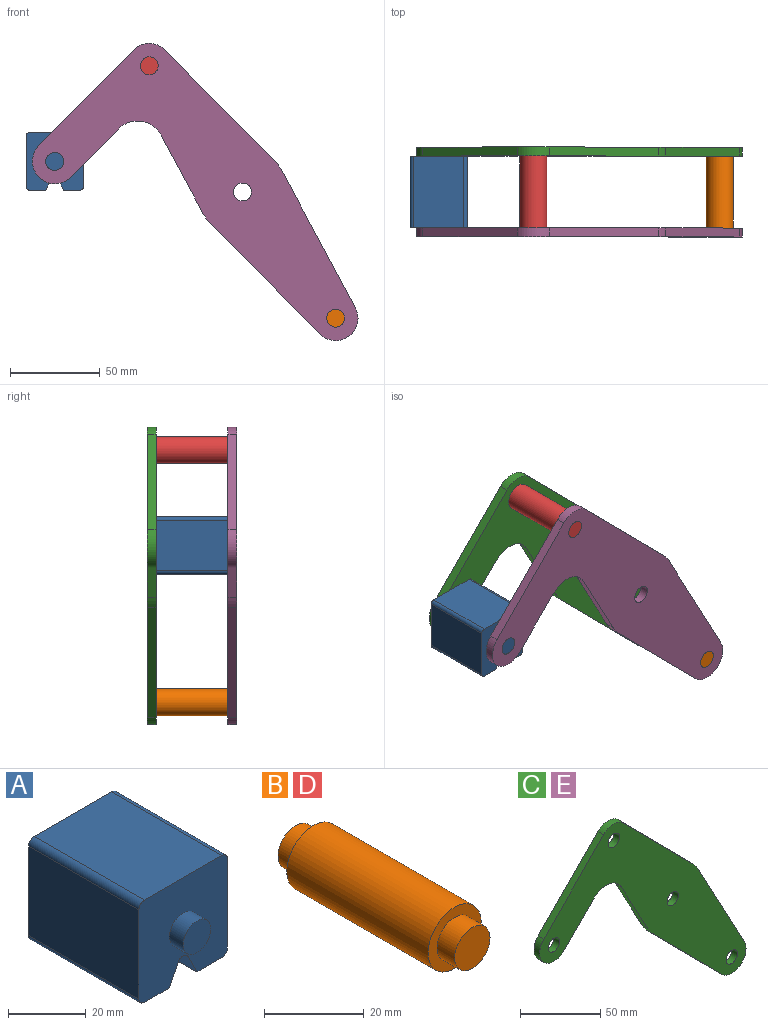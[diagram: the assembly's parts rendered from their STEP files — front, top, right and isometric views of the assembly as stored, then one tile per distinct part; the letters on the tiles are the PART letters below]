
ASSEMBLY  parts=5 mates=3
PART A: 18 faces, bbox 32.1x50x32.1 mm
  f0: plane 40x28.08mm, normal (1,0,0), area 1123.1mm2, adj f4,f10,f13,f14
  f1: plane 40x9.04mm, normal (0,0,-1), area 361.6mm2, adj f2,f4,f10,f14
  f2: plane 40x6.42mm, normal (-0.89,0,-0.45), area 287.2mm2, adj f1,f4,f10,f15
  f3: plane 40x6.42mm, normal (0.89,0,-0.45), area 287.2mm2, adj f4,f5,f10,f15
  f4: plane 32.08x32.08mm, normal (0,-1,0), area 900.6mm2, adj f0,f1,f2,f3,f5,f6,f7,f9
  f5: plane 40x9.04mm, normal (0,0,-1), area 361.6mm2, adj f3,f4,f10,f16
  f6: plane 40x28.08mm, normal (0,0,1), area 1123.1mm2, adj f4,f10,f13,f17
  f7: plane 40x28.08mm, normal (-1,0,0), area 1123.1mm2, adj f4,f10,f16,f17
  f8: plane 10x10mm, normal (0,-1,0), area 78.5mm2, adj f9
  f9: cylinder r=5mm len=10mm, axis (0,1,0), area 157.1mm2, adj f4,f8
  f10: plane 32.08x32.08mm, normal (0,1,0), area 900.6mm2, adj f0,f1,f2,f3,f5,f6,f7,f12
  f11: plane 10x10mm, normal (0,1,0), area 78.5mm2, adj f12
  f12: cylinder r=5mm len=10mm, axis (0,-1,0), area 157.1mm2, adj f10,f11
  f13: cylinder r=2mm len=40mm, axis (0,1,0), area 125.7mm2, adj f0,f4,f6,f10
  f14: cylinder r=2mm len=40mm, axis (0,-1,0), area 125.7mm2, adj f0,f1,f4,f10
  f15: cylinder r=2mm len=40mm, axis (0,1,0), area 177.1mm2, adj f2,f3,f4,f10
  f16: cylinder r=2mm len=40mm, axis (0,1,0), area 125.7mm2, adj f4,f5,f7,f10
  f17: cylinder r=2mm len=40mm, axis (0,-1,0), area 125.7mm2, adj f4,f6,f7,f10
PART B: 7 faces, bbox 15x50x15 mm
  f0: cylinder r=7.5mm len=40mm, axis (0,-1,0), area 1885mm2, adj f2,f5
  f1: cylinder r=5mm len=10mm, axis (0,1,0), area 157.1mm2, adj f2,f3
  f2: plane 15x15mm, normal (0,-1,0), area 98.2mm2, adj f0,f1
  f3: plane 10x10mm, normal (0,-1,0), area 78.5mm2, adj f1
  f4: cylinder r=5mm len=10mm, axis (0,-1,0), area 157.1mm2, adj f5,f6
  f5: plane 15x15mm, normal (0,1,0), area 98.2mm2, adj f0,f4
  f6: plane 10x10mm, normal (0,1,0), area 78.5mm2, adj f4
PART C: 18 faces, bbox 181.7x5x165.8 mm
  f0: plane 43.49x23.35mm, normal (-0.88,0,-0.47), area 246.8mm2, adj f1,f14,f16,f17
  f1: cylinder r=25mm len=5.75mm, axis (0,1,0), area 35.8mm2, adj f0,f2,f16,f17
  f2: plane 61.6x60.87mm, normal (-0.71,0,-0.7), area 433mm2, adj f1,f3,f16,f17
  f3: cylinder r=12.5mm len=21.39mm, axis (0,1,0), area 178.4mm2, adj f2,f4,f16,f17
  f4: plane 76.3x40.96mm, normal (0.88,0,0.47), area 433mm2, adj f3,f5,f16,f17
  f5: cylinder r=25mm len=5.75mm, axis (0,1,0), area 35.8mm2, adj f4,f6,f16,f17
  f6: plane 61.6x60.87mm, normal (0.71,0,0.7), area 433mm2, adj f5,f7,f16,f17
  f7: cylinder r=12.5mm len=17.78mm, axis (0,1,0), area 98.9mm2, adj f6,f8,f16,f17
  f8: plane 53.35x52.71mm, normal (-0.71,0,0.7), area 375mm2, adj f7,f9,f16,f17
  f9: cylinder r=12.5mm len=21.39mm, axis (0,1,0), area 196.3mm2, adj f8,f10,f16,f17
  f10: plane 26.86x26.54mm, normal (0.71,0,-0.7), area 188.8mm2, adj f9,f14,f16,f17
  f11: cylinder r=5mm len=10mm, axis (0,1,0), area 157.1mm2, adj f16,f17
  f12: cylinder r=5mm len=10mm, axis (0,1,0), area 157.1mm2, adj f16,f17
  f13: cylinder r=5mm len=10mm, axis (0,1,0), area 157.1mm2, adj f16,f17
  f14: cylinder r=15mm len=23.89mm, axis (0,1,0), area 140.2mm2, adj f0,f10,f16,f17
  f15: cylinder r=5mm len=10mm, axis (0,1,0), area 157.1mm2, adj f16,f17
  f16: plane 181.66x165.78mm, normal (0,-1,0), area 8710.1mm2, adj f0,f1,f2,f3,f4,f5,f6,f7
  f17: plane 181.66x165.78mm, normal (0,1,0), area 8710.1mm2, adj f0,f1,f2,f3,f4,f5,f6,f7
PART D: same geometry as B
PART E: same geometry as C
PLACE A t=(0,-20,0)mm
PLACE B t=(103.95,-20,-140.78)mm
PLACE C t=(0,25,0)mm
PLACE D t=(0,-20,0)mm
PLACE E t=(0,-20,0)mm fixed
MATE fastened B.f0 <-> E.f3  axis (0,-1,0) through (51.98,-20,-70.39)mm
MATE revolute A.f9 <-> E.f9  axis (0,-1,0) through (-104.69,-25,17.04)mm
MATE fastened D.f0 <-> C.f7  axis (0,1,0) through (-51.98,25,70.39)mm
